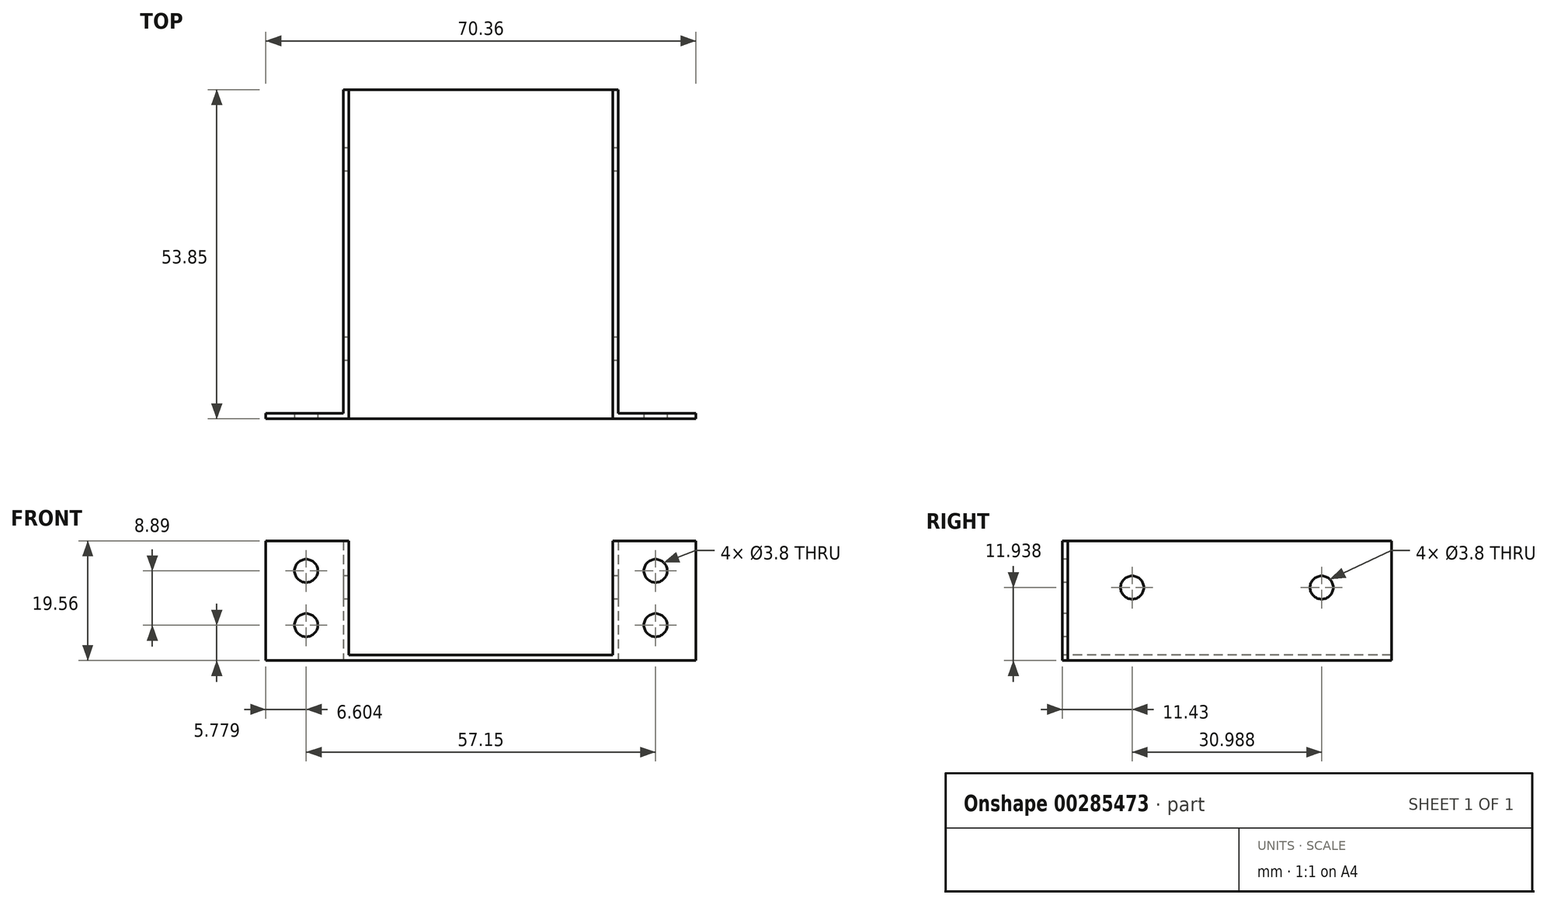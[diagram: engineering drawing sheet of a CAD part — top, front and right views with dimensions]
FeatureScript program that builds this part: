
annotation { "Feature Type Name" : "Feature", "Feature Type Description" : "" }
export const myFeature = defineFeature(function(context is Context, id is Id, definition is map)
    precondition{}
    {
        {
            var Q0;
            Q0=qCreatedBy(makeId("Top.planeOp"),FACE);
            var sketch = newSketch(context, id + "F0", { "sketchPlane" : qUnion([Q0])});
            skLineSegment(sketch, "E0.bottom", {"start": v(0, 0) * mm, "end": v(44.96, 0) * mm});
            skLineSegment(sketch, "E0.top", {"start": v(0, 53.85) * mm, "end": v(44.96, 53.85) * mm});
            skLineSegment(sketch, "E0.left", {"start": v(0, 0) * mm, "end": v(0, 53.85) * mm});
            skLineSegment(sketch, "E0.right", {"start": v(44.96, 0) * mm, "end": v(44.96, 53.85) * mm});
            skSolve(sketch);
        }
        {
            var Q0;
            Q0=qSketchRegion(id+"F0",true);
            extrude(context, id + "F1", {"entities" : qUnion([Q0]), "depth" : 0.89 * mm});
        }
        {
            var Q0;
            Q0=makeQuery(id+"F1.opExtrude","SWEPT_FACE",FACE,{"disambiguationData":[OSD([sQuery(id+"F0.wireOp",EDGE,"E0.bottom")])]});
            var sketch = newSketch(context, id + "F2", { "sketchPlane" : qUnion([Q0])});
            skLineSegment(sketch, "E1.bottom", {"start": v(0, 0.89) * mm, "end": v(0.89, 0.89) * mm});
            skLineSegment(sketch, "E1.top", {"start": v(0, 19.56) * mm, "end": v(0.89, 19.56) * mm});
            skLineSegment(sketch, "E1.left", {"start": v(0, 0.89) * mm, "end": v(0, 19.56) * mm});
            skLineSegment(sketch, "E1.right", {"start": v(0.89, 0.89) * mm, "end": v(0.89, 19.56) * mm});
            skLineSegment(sketch, "E2.bottom", {"start": v(44.96, 0.89) * mm, "end": v(44.07, 0.89) * mm});
            skLineSegment(sketch, "E2.top", {"start": v(44.96, 19.56) * mm, "end": v(44.07, 19.56) * mm});
            skLineSegment(sketch, "E2.left", {"start": v(44.96, 0.89) * mm, "end": v(44.96, 19.56) * mm});
            skLineSegment(sketch, "E2.right", {"start": v(44.07, 0.89) * mm, "end": v(44.07, 19.56) * mm});
            skSolve(sketch);
        }
        {
            var Q0;
            Q0=qSketchRegion(id+"F2",true);
            var Q1;
            Q1=makeQuery(id+"F1.opExtrude","SWEPT_FACE",FACE,{"disambiguationData":[OSD([sQuery(id+"F0.wireOp",EDGE,"E0.top")])]});
            extrude(context, id + "F3", {"entities" : qUnion([Q0]), "operationType" : NewBodyOperationType.ADD, "endBound" : BoundingType.UP_TO_SURFACE, "oppositeDirection" : true, "endBoundEntityFace" : qUnion([Q1]), "depth" : 25.4 * mm});
        }
        {
            var Q0;
            Q0=makeQuery(id+"F3.boolean.opBoolean","MERGE",FACE,{"derivedFrom":[makeQuery(id+"F1.opExtrude","SWEPT_FACE",FACE,{"disambiguationData":[OSD([sQuery(id+"F0.wireOp",EDGE,"E0.left")])]}),makeQuery(id+"F3.opExtrude","SWEPT_FACE",FACE,{"disambiguationData":[OSD([sQuery(id+"F2.wireOp",EDGE,"E1.left")])]})]});
            var sketch = newSketch(context, id + "F4", { "sketchPlane" : qUnion([Q0])});
            skLineSegment(sketch, "E3.bottom", {"start": v(0, 19.56) * mm, "end": v(-0.89, 19.56) * mm});
            skLineSegment(sketch, "E3.top", {"start": v(0, 0) * mm, "end": v(-0.89, 0) * mm});
            skLineSegment(sketch, "E3.left", {"start": v(0, 19.56) * mm, "end": v(0, 0) * mm});
            skLineSegment(sketch, "E3.right", {"start": v(-0.89, 19.56) * mm, "end": v(-0.89, 0) * mm});
            skSolve(sketch);
        }
        {
            var Q0;
            Q0=qSketchRegion(id+"F4",true);
            extrude(context, id + "F5", {"entities" : qUnion([Q0]), "operationType" : NewBodyOperationType.ADD, "depth" : 12.7 * mm});
        }
        {
            var Q0;
            Q0=makeQuery(id+"F3.boolean.opBoolean","MERGE",FACE,{"derivedFrom":[makeQuery(id+"F1.opExtrude","SWEPT_FACE",FACE,{"disambiguationData":[OSD([sQuery(id+"F0.wireOp",EDGE,"E0.right")])]}),makeQuery(id+"F3.opExtrude","SWEPT_FACE",FACE,{"disambiguationData":[OSD([sQuery(id+"F2.wireOp",EDGE,"E2.left")])]})]});
            var sketch = newSketch(context, id + "F6", { "sketchPlane" : qUnion([Q0])});
            skLineSegment(sketch, "E4.bottom", {"start": v(0, 19.56) * mm, "end": v(0.89, 19.56) * mm});
            skLineSegment(sketch, "E4.top", {"start": v(0, 0) * mm, "end": v(0.89, 0) * mm});
            skLineSegment(sketch, "E4.left", {"start": v(0, 19.56) * mm, "end": v(0, 0) * mm});
            skLineSegment(sketch, "E4.right", {"start": v(0.89, 19.56) * mm, "end": v(0.89, 0) * mm});
            skSolve(sketch);
        }
        {
            var Q0;
            Q0=qSketchRegion(id+"F6",true);
            extrude(context, id + "F7", {"entities" : qUnion([Q0]), "operationType" : NewBodyOperationType.ADD, "depth" : 12.7 * mm});
        }
        {
            var Q0;
            Q0=makeQuery(id+"F7.boolean.opBoolean","MERGE",FACE,{"derivedFrom":[makeQuery(id+"F5.boolean.opBoolean","MERGE",FACE,{"derivedFrom":[makeQuery(id+"F3.boolean.opBoolean","MERGE",FACE,{"derivedFrom":[makeQuery(id+"F1.opExtrude","SWEPT_FACE",FACE,{"disambiguationData":[OSD([sQuery(id+"F0.wireOp",EDGE,"E0.bottom")])]}),makeQuery(id+"F3.opExtrude","CAP_FACE",FACE,{"disambiguationData":[OSD([sQuery(id+"F2.wireOp",EDGE,"E1.bottom"),sQuery(id+"F2.wireOp",EDGE,"E1.top"),sQuery(id+"F2.wireOp",EDGE,"E1.left"),sQuery(id+"F2.wireOp",EDGE,"E1.right")])],"isStart":true}),makeQuery(id+"F3.opExtrude","CAP_FACE",FACE,{"disambiguationData":[OSD([sQuery(id+"F2.wireOp",EDGE,"E2.bottom"),sQuery(id+"F2.wireOp",EDGE,"E2.top"),sQuery(id+"F2.wireOp",EDGE,"E2.left"),sQuery(id+"F2.wireOp",EDGE,"E2.right")])],"isStart":true})]}),makeQuery(id+"F5.opExtrude","SWEPT_FACE",FACE,{"disambiguationData":[OSD([sQuery(id+"F4.wireOp",EDGE,"E3.left")])]})]}),makeQuery(id+"F7.opExtrude","SWEPT_FACE",FACE,{"disambiguationData":[OSD([sQuery(id+"F6.wireOp",EDGE,"E4.left")])]})]});
            var sketch = newSketch(context, id + "F8", { "sketchPlane" : qUnion([Q0])});
            skPoint(sketch, "E5", {"position": v(-6.1, 14.67) * mm});
            skPoint(sketch, "E6", {"position": v(-6.1, 5.78) * mm});
            skPoint(sketch, "E7", {"position": v(51.05, 14.67) * mm});
            skPoint(sketch, "E8", {"position": v(51.05, 5.78) * mm});
            skLineSegment(sketch, "E9", {"start": v(-6.1, 19.56) * mm, "end": v(-6.1, 0) * mm, "construction": true});
            skLineSegment(sketch, "E10", {"start": v(51.05, 19.56) * mm, "end": v(51.05, 0) * mm, "construction": true});
            skCircle(sketch, "E11", {"center": v(-6.1, 14.67) * mm, "radius": 2.03 * mm, "construction": true});
            skCircle(sketch, "E12", {"center": v(-6.1, 5.78) * mm, "radius": 2.03 * mm, "construction": true});
            skCircle(sketch, "E13", {"center": v(51.05, 5.78) * mm, "radius": 2.03 * mm, "construction": true});
            skCircle(sketch, "E14", {"center": v(51.05, 14.67) * mm, "radius": 2.03 * mm, "construction": true});
            skLineSegment(sketch, "E15", {"start": v(0.89, 10.22) * mm, "end": v(-12.7, 10.22) * mm, "construction": true});
            skSolve(sketch);
        }
        {
            var Q0;
            Q0=sQuery(id+"F8.wireOp",VERTEX,"E5");
            var Q1;
            Q1=sQuery(id+"F8.wireOp",VERTEX,"E6");
            var Q2;
            Q2=sQuery(id+"F8.wireOp",VERTEX,"E8");
            var Q3;
            Q3=sQuery(id+"F8.wireOp",VERTEX,"E7");
            var Q4;
            Q4=makeQuery(id+"F1.opExtrude","SWEPT_BODY",BODY,{"disambiguationData":[OSD([sQuery(id+"F0.wireOp",EDGE,"E0.bottom"),sQuery(id+"F0.wireOp",EDGE,"E0.top"),sQuery(id+"F0.wireOp",EDGE,"E0.left"),sQuery(id+"F0.wireOp",EDGE,"E0.right")])]});
            hole(context, id + "F9", {"style" : HoleStyle.SIMPLE, "endStyle" : HoleEndStyle.THROUGH, "standardTappedOrClearance" : lookupTablePath({ "standard" : "ANSI", "fit" : "Normal (ASME)", "size" : "#6", "type" : "Clearance" }), "standardBlindInLast" : lookupTablePath({ "fit" : "Free", "standard" : "ANSI", "size" : "#6", "type" : "Clearance" }), "holeDiameter" : 3.8 * mm, "isTappedThrough" : true, "tappedDepth" : 2.77 * mm, "tapClearance" : 3, "startFromSketch" : true, "locations" : qUnion([Q0, Q1, Q2, Q3]), "scope" : qUnion([Q4])});
        }
        {
            var Q0;
            Q0=makeQuery(id+"F3.boolean.opBoolean","MERGE",FACE,{"derivedFrom":[makeQuery(id+"F1.opExtrude","SWEPT_FACE",FACE,{"disambiguationData":[OSD([sQuery(id+"F0.wireOp",EDGE,"E0.left")])]}),makeQuery(id+"F3.opExtrude","SWEPT_FACE",FACE,{"disambiguationData":[OSD([sQuery(id+"F2.wireOp",EDGE,"E1.left")])]})]});
            var sketch = newSketch(context, id + "F10", { "sketchPlane" : qUnion([Q0])});
            skPoint(sketch, "E16", {"position": v(-11.43, 11.94) * mm});
            skPoint(sketch, "E17", {"position": v(-42.42, 11.94) * mm});
            skSolve(sketch);
        }
        {
            var Q0;
            Q0=sQuery(id+"F10.wireOp",VERTEX,"d304fd5c-6220-4145-91d9-950adf901c65");
            var Q1;
            Q1=sQuery(id+"F10.wireOp",VERTEX,"E16");
            var Q2;
            Q2=sQuery(id+"F10.wireOp",VERTEX,"E17");
            var Q3;
            Q3=makeQuery(id+"F1.opExtrude","SWEPT_BODY",BODY,{"disambiguationData":[OSD([sQuery(id+"F0.wireOp",EDGE,"E0.bottom"),sQuery(id+"F0.wireOp",EDGE,"E0.top"),sQuery(id+"F0.wireOp",EDGE,"E0.left"),sQuery(id+"F0.wireOp",EDGE,"E0.right")])]});
            hole(context, id + "F11", {"style" : HoleStyle.SIMPLE, "endStyle" : HoleEndStyle.THROUGH, "standardTappedOrClearance" : lookupTablePath({ "standard" : "ANSI", "fit" : "Normal (ASME)", "size" : "#6", "type" : "Clearance" }), "standardBlindInLast" : lookupTablePath({ "fit" : "Free", "standard" : "ANSI", "size" : "#6", "type" : "Clearance" }), "holeDiameter" : 3.8 * mm, "isTappedThrough" : true, "tappedDepth" : 2.77 * mm, "tapClearance" : 3, "startFromSketch" : true, "locations" : qUnion([Q0, Q1, Q2]), "scope" : qUnion([Q3])});
        }
    });
